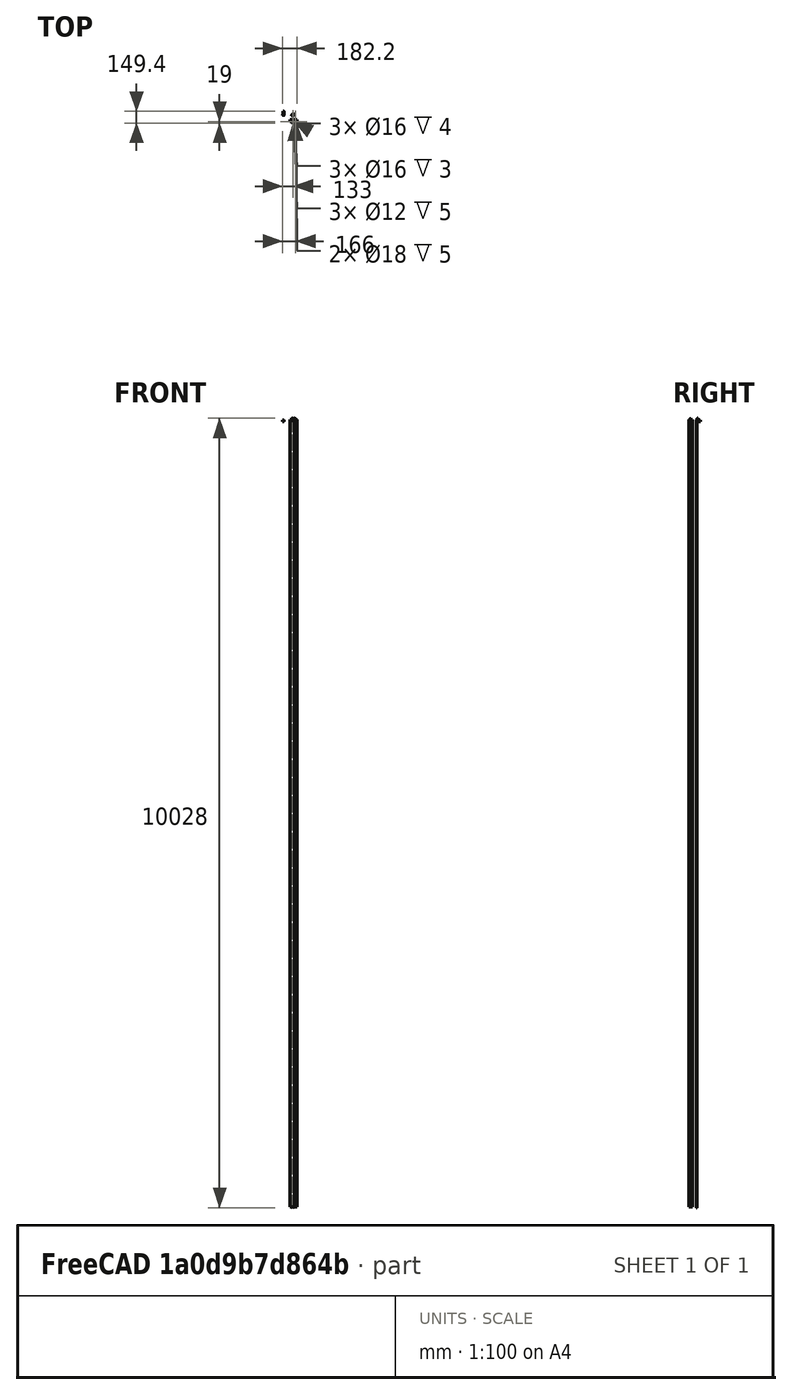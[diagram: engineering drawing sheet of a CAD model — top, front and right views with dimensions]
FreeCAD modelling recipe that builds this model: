
FCSTD DOCUMENT  (FreeCAD 0.15R4671 (Git))
Label: XCarrage_RetainerClip_AluRepRap_3DA-002
License: All rights reserved
LicenseURL: http://en.wikipedia.org/wiki/All_rights_reserved
objects: Sketcher::SketchObject×17, PartDesign::Pocket×13, PartDesign::Fillet×7, Mesh::Feature×5, Part::Feature×4, PartDesign::Pad×3, PartDesign::Chamfer×1
note: 61 computed .brp shape members not serialized (recipe doc carries the construction recipe); baked Part::Feature solids carry a one-line shape summary decoded from their .brp

FEATURE [Sketcher::SketchObject] Sketch
  Placement = pos=(0,-58,0) rot=(1,0,0;1.5708rad)
  sketch-geometry (4):
    g0: LineSegment StartX=93 StartY=-10 StartZ=0 EndX=149 EndY=-10 EndZ=0
    g1: LineSegment StartX=149 StartY=-10 StartZ=0 EndX=149 EndY=18 EndZ=0
    g2: LineSegment StartX=149 StartY=18 StartZ=0 EndX=93 EndY=18 EndZ=0
    g3: LineSegment StartX=93 StartY=18 StartZ=0 EndX=93 EndY=-10 EndZ=0
  constraints (8):
    c: Coincident(g0,g1)
    c: Coincident(g1,g2)
    c: Coincident(g2,g3)
    c: Coincident(g3,g0)
    c: Horizontal(g0)
    c: Horizontal(g2)
    c: Vertical(g1)
    c: Vertical(g3)
FEATURE [PartDesign::Pad] Pad
  Length = 5
  Length2 = 100
  Placement = pos=(0,-58,0) rot=(1,0,0;1.5708rad)
  Sketch = -> Sketch
  Type = 0
FEATURE [Mesh::Feature] HexHotEnd  label="HexHotEnd1"
  Placement = pos=(122,-78,-20) rot=(0,0,1;0rad)
FEATURE [Mesh::Feature] PNEUMATIC_NIPPLE
  Placement = pos=(111,-50,-28) rot=(0,-1,0;1.5708rad)
FEATURE [Part::Feature] Part__Feature  label="LJ18A3"
  Placement = pos=(155,-78,-52) rot=(0,0,1;0rad)
  shape: bbox 17.85 x 17.85 x 79.1 mm, 11 faces (baked)
FEATURE [Mesh::Feature] Hotend_Dummy___GTMax3D  label="Hotend_Dummy_-_GTMax3D"
  Placement = pos=(173,-78,-48.4) rot=(0,0,1;0rad)
FEATURE [Sketcher::SketchObject] Sketch001
  Placement = pos=(0,-63,0) rot=(1,0,0;1.5708rad)
  Support = -> Pad [Face6]
  sketch-geometry (4):
    g0: LineSegment StartX=161 StartY=18 StartZ=0 EndX=149 EndY=18 EndZ=0
    g1: LineSegment StartX=149 StartY=18 StartZ=0 EndX=149 EndY=-53.76 EndZ=0
    g2: LineSegment StartX=149 StartY=-53.76 StartZ=0 EndX=161 EndY=-53.76 EndZ=0
    g3: LineSegment StartX=161 StartY=-53.76 StartZ=0 EndX=161 EndY=18 EndZ=0
  constraints (9):
    c: Coincident(g0,g1)
    c: Coincident(g1,g2)
    c: Coincident(g2,g3)
    c: Coincident(g3,g0)
    c: Horizontal(g0)
    c: Horizontal(g2)
    c: Vertical(g1)
    c: Vertical(g3)
    c: DistanceY(g2,g0) = 71.76
FEATURE [Part::Feature] Part__Feature001  label="JHead_Nozzle"
  shape: bbox 17.41 x 24.4 x 17.41 mm, 34 faces (baked)
FEATURE [Part::Feature] Part__Feature002  label="JHead_Nozzle001"
  shape: bbox 16 x 40 x 16 mm, 230 faces (baked)
FEATURE [Sketcher::SketchObject] Sketch002
  Placement = pos=(0,-63,0) rot=(1,0,0;1.5708rad)
  Support = -> Pad [Face6]
  sketch-geometry (4):
    g0: LineSegment StartX=104 StartY=18 StartZ=0 EndX=138 EndY=18 EndZ=0
    g1: LineSegment StartX=138 StartY=18 StartZ=0 EndX=138 EndY=6 EndZ=0
    g2: LineSegment StartX=138 StartY=6 StartZ=0 EndX=104 EndY=6 EndZ=0
    g3: LineSegment StartX=104 StartY=6 StartZ=0 EndX=104 EndY=18 EndZ=0
  constraints (9):
    c: Coincident(g0,g1)
    c: Coincident(g1,g2)
    c: Coincident(g2,g3)
    c: Coincident(g3,g0)
    c: Horizontal(g0)
    c: Horizontal(g2)
    c: Vertical(g1)
    c: Vertical(g3)
    c: DistanceY(g2,g0) = 12
FEATURE [PartDesign::Pad] Pad001
  Length = 28
  Length2 = 100
  Placement = pos=(0,-58,0) rot=(1,0,0;1.5708rad)
  Sketch = -> Sketch002
  Type = 0
FEATURE [Sketcher::SketchObject] Sketch003
  Placement = pos=(0,-58,18) rot=(0,0,1;3.14159rad)
  Support = -> Pad001 [Face10]
  sketch-geometry (1):
    g0: Circle CenterX=-122 CenterY=20 CenterZ=0 NormalX=0 NormalY=0 NormalZ=1 Radius=8
  constraints (1):
    c: Radius(g0) = 8
FEATURE [PartDesign::Pocket] Pocket
  Length = 4
  Placement = pos=(0,-58,0) rot=(1,0,0;1.5708rad)
  Sketch = -> Sketch003
  Type = 0
FEATURE [Sketcher::SketchObject] Sketch004
  Placement = pos=(0,-58,14) rot=(0,0,1;3.14159rad)
  Support = -> Pocket [Face12]
  sketch-geometry (1):
    g0: Circle CenterX=-122 CenterY=20 CenterZ=0 NormalX=0 NormalY=0 NormalZ=1 Radius=6
  constraints (1):
    c: Radius(g0) = 6
FEATURE [PartDesign::Pocket] Pocket001
  Length = 5
  Placement = pos=(0,-58,0) rot=(1,0,0;1.5708rad)
  Sketch = -> Sketch004
  Type = 0
FEATURE [Sketcher::SketchObject] Sketch005
  Placement = pos=(0,-58,6) rot=(1,0,0;3.14159rad)
  Support = -> Pocket001 [Face8]
  sketch-geometry (1):
    g0: Circle CenterX=122 CenterY=20 CenterZ=0 NormalX=0 NormalY=0 NormalZ=1 Radius=8
  constraints (1):
    c: Radius(g0) = 8
FEATURE [PartDesign::Pocket] Pocket002
  Length = 3
  Placement = pos=(0,-58,0) rot=(1,0,0;1.5708rad)
  Sketch = -> Sketch005
  Type = 0
FEATURE [Sketcher::SketchObject] Sketch006
  Placement = pos=(0,-58,0) rot=(-1,0,0;1.5708rad)
  Support = -> Pocket002 [Face4]
  sketch-geometry (4):
    g0: LineSegment StartX=142 StartY=10 StartZ=0 EndX=168 EndY=10 EndZ=0
    g1: LineSegment StartX=168 StartY=10 StartZ=0 EndX=168 EndY=5 EndZ=0
    g2: LineSegment StartX=168 StartY=5 StartZ=0 EndX=142 EndY=5 EndZ=0
    g3: LineSegment StartX=142 StartY=5 StartZ=0 EndX=142 EndY=10 EndZ=0
  constraints (8):
    c: Coincident(g0,g1)
    c: Coincident(g1,g2)
    c: Coincident(g2,g3)
    c: Coincident(g3,g0)
    c: Horizontal(g0)
    c: Horizontal(g2)
    c: Vertical(g1)
    c: Vertical(g3)
FEATURE [PartDesign::Pad] Pad002
  Length = 33
  Length2 = 100
  Placement = pos=(0,-58,0) rot=(1,0,0;1.5708rad)
  Reversed = true
  Sketch = -> Sketch006
  Type = 0
FEATURE [PartDesign::Chamfer] Chamfer
  Base = -> Pad002 [Edge21]
  Placement = pos=(0,-58,0) rot=(1,0,0;1.5708rad)
  Size = 18.99
FEATURE [PartDesign::Fillet] Fillet
  Base = -> Chamfer [Edge34,Edge46]
  Placement = pos=(0,-58,0) rot=(1,0,0;1.5708rad)
  Radius = 12.99
FEATURE [PartDesign::Fillet] Fillet001
  Base = -> Fillet [Edge32]
  Placement = pos=(0,-58,0) rot=(1,0,0;1.5708rad)
  Radius = 10
FEATURE [PartDesign::Fillet] Fillet002
  Base = -> Fillet001 [Edge25,Edge22]
  Placement = pos=(0,-58,0) rot=(1,0,0;1.5708rad)
  Radius = 4
FEATURE [Sketcher::SketchObject] Sketch007
  Placement = pos=(0,-58,-5) rot=(0,0,1;3.14159rad)
  Support = -> Fillet002 [Face8]
  sketch-geometry (1):
    g0: Circle CenterX=-155 CenterY=20 CenterZ=0 NormalX=0 NormalY=0 NormalZ=1 Radius=9
  constraints (1):
    c: Radius(g0) = 9
FEATURE [PartDesign::Pocket] Pocket003
  Length = 5
  Placement = pos=(0,-58,0) rot=(1,0,0;1.5708rad)
  Sketch = -> Sketch007
  Type = 0
FEATURE [PartDesign::Fillet] Fillet003
  Base = -> Pocket003 [Edge13]
  Placement = pos=(0,-58,0) rot=(1,0,0;1.5708rad)
  Radius = 2
FEATURE [PartDesign::Fillet] Fillet004
  Base = -> Fillet003 [Edge25,Edge32]
  Placement = pos=(0,-58,0) rot=(1,0,0;1.5708rad)
  Radius = 2
FEATURE [Sketcher::SketchObject] Sketch008
  Placement = pos=(0,-63,0) rot=(1,0,0;1.5708rad)
  Support = -> Fillet004 [Face1]
  sketch-geometry (2):
    g0: Circle CenterX=107 CenterY=1 CenterZ=0 NormalX=0 NormalY=0 NormalZ=1 Radius=1.8
    g1: Circle CenterX=132 CenterY=1 CenterZ=0 NormalX=0 NormalY=0 NormalZ=1 Radius=1.8
  constraints (5):
    c: DistanceX(g0,g1) = 25
    c: DistanceX(g0) = 107
    c: DistanceY(g0) = 1
    c: Radius(g0) = 1.8
    c: Equal(g0,g1)
FEATURE [PartDesign::Pocket] Pocket004
  Length = 5
  Placement = pos=(0,-58,0) rot=(1,0,0;1.5708rad)
  Sketch = -> Sketch008
  Type = 1
FEATURE [Sketcher::SketchObject] Sketch009
  Placement = pos=(0,-63,0) rot=(1,0,0;1.5708rad)
  Support = -> Pocket004 [Face1]
  sketch-geometry (2):
    g0: Circle CenterX=107 CenterY=1 CenterZ=0 NormalX=0 NormalY=0 NormalZ=1 Radius=3.6
    g1: Circle CenterX=132 CenterY=1 CenterZ=0 NormalX=0 NormalY=0 NormalZ=1 Radius=3.6
  constraints (2):
    c: Radius(g1) = 3.6
    c: Equal(g1,g0)
FEATURE [PartDesign::Pocket] Pocket005
  Length = 3
  Placement = pos=(0,-58,0) rot=(1,0,0;1.5708rad)
  Sketch = -> Sketch009
  Type = 0
FEATURE [Mesh::Feature] HexNutStyle1_M  label="HexNutStyle1_M3"
  Placement = pos=(123,43,34) rot=(1,0,0;1.5708rad)
FEATURE [Mesh::Feature] HexNutStyle1_M001  label="HexNutStyle1_M004"
  Placement = pos=(148,43,34) rot=(1,0,0;1.5708rad)
FEATURE [Sketcher::SketchObject] Sketch010
  Placement = pos=(0,-91,0) rot=(1,0,0;1.5708rad)
  Support = -> Pocket005 [Face19]
  sketch-geometry (2):
    g0: Circle CenterX=108.75 CenterY=12 CenterZ=0 NormalX=0 NormalY=0 NormalZ=1 Radius=1.8
    g1: Circle CenterX=133.75 CenterY=12 CenterZ=0 NormalX=0 NormalY=0 NormalZ=1 Radius=1.8
  constraints (2):
    c: Radius(g0) = 1.8
    c: Equal(g0,g1)
FEATURE [PartDesign::Pocket] Pocket006
  Length = 21
  Placement = pos=(0,-58,0) rot=(1,0,0;1.5708rad)
  Sketch = -> Sketch010
  Type = 0
FEATURE [Sketcher::SketchObject] Sketch011
  Placement = pos=(0,-91,0) rot=(1,0,0;1.5708rad)
  Support = -> Pocket006 [Face19]
  sketch-geometry (2):
    g0: Circle CenterX=133.75 CenterY=12 CenterZ=0 NormalX=0 NormalY=0 NormalZ=1 Radius=3.5
    g1: Circle CenterX=108.75 CenterY=12 CenterZ=0 NormalX=0 NormalY=0 NormalZ=1 Radius=3.5
  constraints (2):
    c: Radius(g0) = 3.5
    c: Equal(g0,g1)
FEATURE [PartDesign::Pocket] Pocket007
  Length = 11
  Placement = pos=(0,-58,0) rot=(1,0,0;1.5708rad)
  Sketch = -> Sketch011
  Type = 0
FEATURE [Sketcher::SketchObject] Sketch012
  Placement = pos=(0,-58,18) rot=(0,0,1;3.14159rad)
  Support = -> Pocket007 [Face5]
  sketch-geometry (6):
    g0: LineSegment StartX=-140 StartY=29 StartZ=0 EndX=-129 EndY=29 EndZ=0
    g1: LineSegment StartX=-115 StartY=29 StartZ=0 EndX=-102 EndY=29 EndZ=0
    g2: ArcOfCircle CenterX=-122 CenterY=20 CenterZ=0 NormalX=0 NormalY=0 NormalZ=1 Radius=11.4018 StartAngle=0.909753 EndAngle=2.23184
    g3: LineSegment StartX=-140 StartY=29 StartZ=0 EndX=-140 EndY=34 EndZ=0
    g4: LineSegment StartX=-140 StartY=34 StartZ=0 EndX=-102 EndY=34 EndZ=0
    g5: LineSegment StartX=-102 StartY=34 StartZ=0 EndX=-102 EndY=29 EndZ=0
  constraints (5):
    c: Coincident(g3,g4)
    c: Coincident(g4,g5)
    c: Coincident(g0,g2)
    c: Coincident(g1,g2)
    c: Coincident(g1,g5)
FEATURE [PartDesign::Pocket] Pocket008
  Length = 5
  Placement = pos=(0,-58,0) rot=(1,0,0;1.5708rad)
  Sketch = -> Sketch012
  Type = 1
FEATURE [PartDesign::Fillet] Fillet005
  Base = -> Pocket008 [Edge84,Edge88]
  Placement = pos=(0,-58,0) rot=(1,0,0;1.5708rad)
  Radius = 1
FEATURE [Part::Feature] Fillet006  label="XCarrage_Retainer_AluRepRap_3DA-002"
  shape: bbox 75 x 33 x 28 mm, 50 faces (baked)
FEATURE [Sketcher::SketchObject] Sketch013
  Placement = pos=(0,0,18) rot=(0,0,1;0rad)
  Support = -> Fillet006 [Face1]
  sketch-geometry (6):
    g0: LineSegment StartX=85 StartY=-78.25 StartZ=0 EndX=140 EndY=-78.25 EndZ=0
    g1: LineSegment StartX=140 StartY=-78.25 StartZ=0 EndX=140 EndY=-97 EndZ=0
    g2: LineSegment StartX=140 StartY=-97 StartZ=0 EndX=171.204 EndY=-97 EndZ=0
    g3: LineSegment StartX=171.204 StartY=-97 StartZ=0 EndX=171.204 EndY=-53.4803 EndZ=0
    g4: LineSegment StartX=171.204 StartY=-53.4803 StartZ=0 EndX=85 EndY=-53.4803 EndZ=0
    g5: LineSegment StartX=85 StartY=-53.4803 StartZ=0 EndX=85 EndY=-78.25 EndZ=0
  constraints (12):
    c: Coincident(g0,g1)
    c: Coincident(g1,g2)
    c: Coincident(g2,g3)
    c: Coincident(g3,g4)
    c: Coincident(g4,g5)
    c: Coincident(g0,g5)
    c: Vertical(g5)
    c: Vertical(g3)
    c: Vertical(g1)
    c: Horizontal(g0)
    c: Horizontal(g4)
    c: Horizontal(g2)
FEATURE [PartDesign::Pocket] Pocket009  label="HotendRetainerClip"
  Length = 5
  Sketch = -> Sketch013
  Type = 1
FEATURE [Sketcher::SketchObject] Sketch014
  Placement = pos=(0,0,18) rot=(0,0,1;0rad)
  Support = -> Pocket009 [Face1]
  sketch-geometry (1):
    g0: Circle CenterX=122 CenterY=-78 CenterZ=0 NormalX=0 NormalY=0 NormalZ=1 Radius=8.2
  constraints (1):
    c: Radius(g0) = 8.2
FEATURE [PartDesign::Pocket] Pocket010
  Length = 4.2
  Sketch = -> Sketch014
  Type = 0
FEATURE [Sketcher::SketchObject] Sketch015
  Placement = pos=(0,0,6) rot=(1,0,0;3.14159rad)
  Support = -> Pocket010 [Face12]
  sketch-geometry (1):
    g0: Circle CenterX=122 CenterY=78 CenterZ=0 NormalX=0 NormalY=0 NormalZ=1 Radius=8.2
  constraints (1):
    c: Radius(g0) = 8.2
FEATURE [PartDesign::Pocket] Pocket011
  Length = 3.2
  Sketch = -> Sketch015
  Type = 0
FEATURE [Sketcher::SketchObject] Sketch016
  Placement = pos=(0,0,9.2) rot=(1,0,0;3.14159rad)
  Support = -> Pocket011 [Face20]
  sketch-geometry (1):
    g0: Circle CenterX=122 CenterY=78 CenterZ=0 NormalX=0 NormalY=0 NormalZ=1 Radius=6.2
  constraints (1):
    c: Radius(g0) = 6.2
FEATURE [PartDesign::Pocket] Pocket012
  Length = 5
  Sketch = -> Sketch016
  Type = 0
FEATURE [PartDesign::Fillet] Fillet007  label="XCarrage_Retainer_AluRepRap_3DA-003"
  Base = -> Pocket012 [Edge58,Edge57,Edge9,Edge48]
  Radius = 0.5
